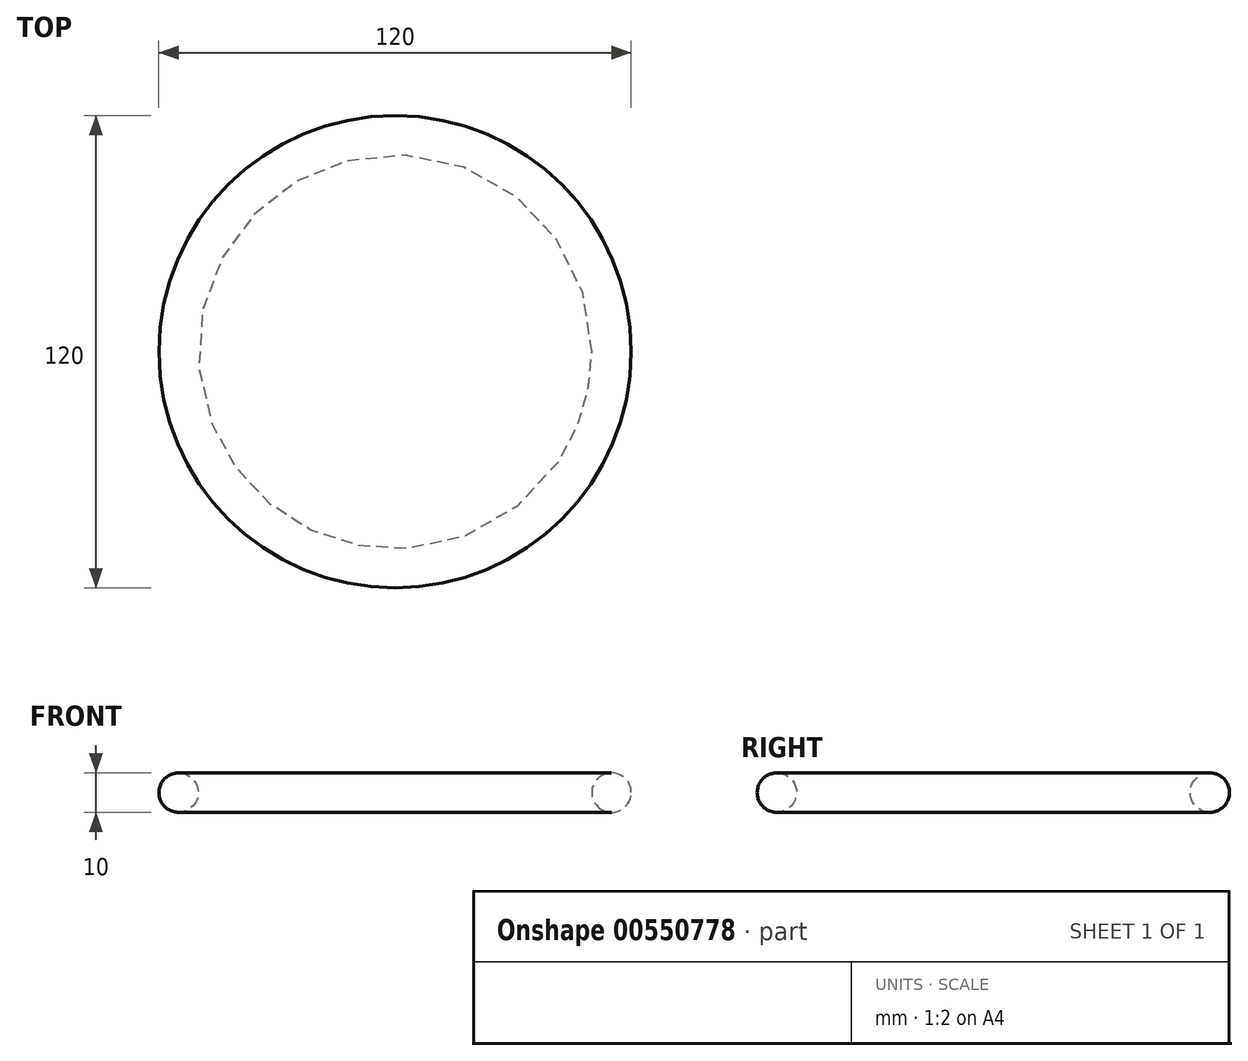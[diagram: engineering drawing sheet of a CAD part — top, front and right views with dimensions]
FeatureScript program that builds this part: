
annotation { "Feature Type Name" : "Feature", "Feature Type Description" : "" }
export const myFeature = defineFeature(function(context is Context, id is Id, definition is map)
    precondition{}
    {
        {
            var Q0;
            Q0=qCreatedBy(makeId("Top.planeOp"),FACE);
            var sketch = newSketch(context, id + "F0", { "sketchPlane" : qUnion([Q0])});
            skCircle(sketch, "E0", {"center": v(-48.89, 39.3) * mm, "radius": 50 * mm});
            skCircle(sketch, "E1.0", {"center": v(-48.89, 39.3) * mm, "radius": 60 * mm});
            skSolve(sketch);
        }
        {
            var Q0;
            Q0 = qSketchRegion(id + "F0", true);
            extrude(context, id + "F1", {"entities" : qUnion([Q0]), "depth" : 10 * mm, "offsetDistance" : 25 * mm});
        }
        {
            var Q0;
            Q0=makeQuery(id+"F1.opExtrude","CAP_EDGE",EDGE,{"disambiguationData":[OSD([sQuery(id+"F0.wireOp",EDGE,"E1.0")])],"isStart":false});
            var Q1;
            Q1=makeQuery(id+"F1.opExtrude","CAP_EDGE",EDGE,{"disambiguationData":[OSD([sQuery(id+"F0.wireOp",EDGE,"E1.0")])],"isStart":true});
            var Q2;
            Q2=makeQuery(id+"F1.opExtrude","CAP_EDGE",EDGE,{"disambiguationData":[OSD([sQuery(id+"F0.wireOp",EDGE,"E0")])],"isStart":false});
            var Q3;
            Q3=makeQuery(id+"F1.opExtrude","CAP_EDGE",EDGE,{"disambiguationData":[OSD([sQuery(id+"F0.wireOp",EDGE,"E0")])],"isStart":true});
            fillet(context, id + "F2", {"entities" : qUnion([Q0, Q1, Q2, Q3]), "radius" : 5 * mm, "tangentPropagation" : true, "allowEdgeOverflow" : false});
        }
    });
